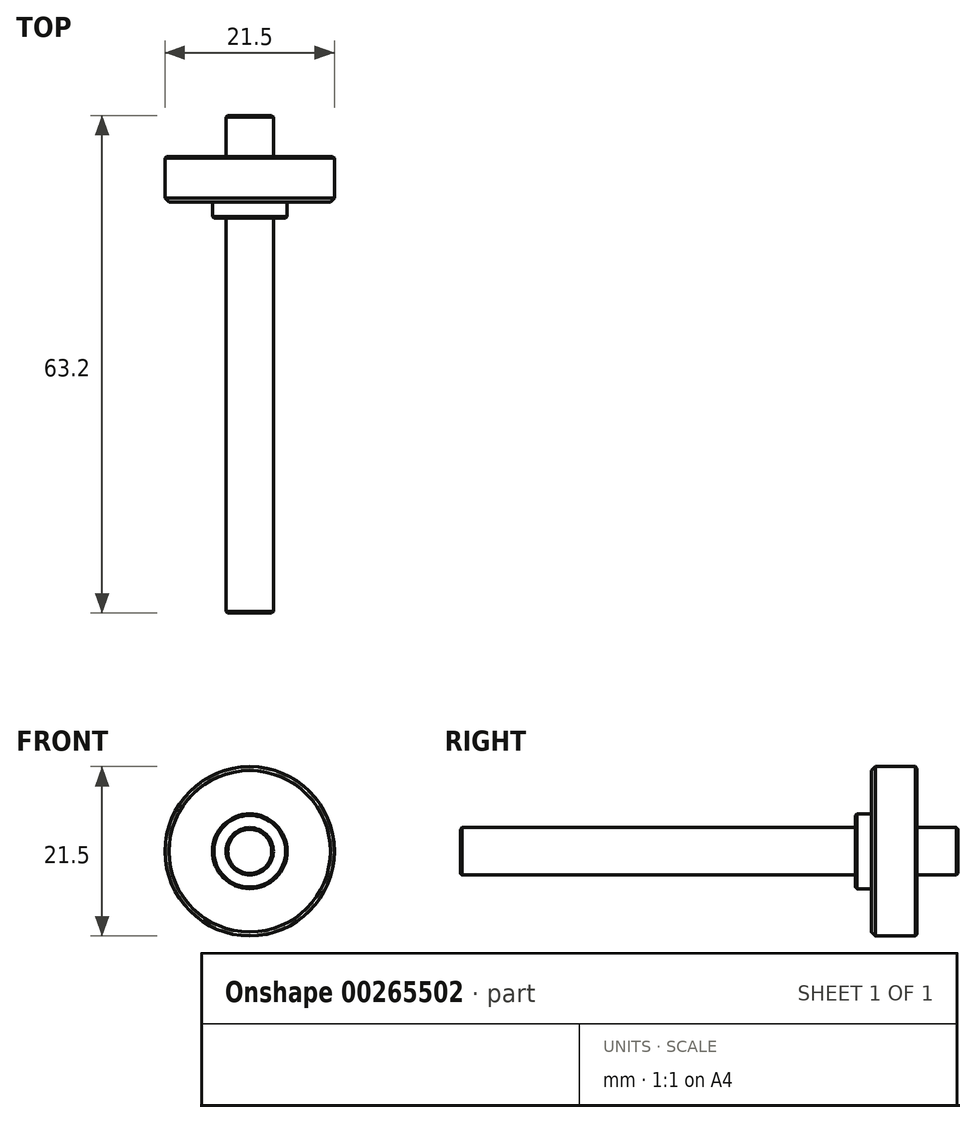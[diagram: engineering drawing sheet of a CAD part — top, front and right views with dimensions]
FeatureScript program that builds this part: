
annotation { "Feature Type Name" : "Feature", "Feature Type Description" : "" }
export const myFeature = defineFeature(function(context is Context, id is Id, definition is map)
    precondition{}
    {
        {
            var Q0;
            Q0=qCreatedBy(makeId("Front.planeOp"),FACE);
            var sketch = newSketch(context, id + "F0", { "sketchPlane" : qUnion([Q0])});
            skCircle(sketch, "E0", {"center": v(0, 0) * mm, "radius": 10.75 * mm});
            skSolve(sketch);
        }
        {
            var Q0;
            Q0=makeQuery(id+"F0.imprint","IMPRINT",FACE,{"disambiguationData":[TD([[makeQuery(id+"F0.imprint","IMPRINT",EDGE,{"derivedFrom":sQuery(id+"F0.wireOp",EDGE,"E0")}),1.0]])]});
            extrude(context, id + "F1", {"entities" : qUnion([Q0]), "depth" : 5.8 * mm});
        }
        {
            var Q0;
            Q0=makeQuery(id+"F1.opExtrude","CAP_FACE",FACE,{"disambiguationData":[OSD([sQuery(id+"F0.wireOp",EDGE,"E0")])],"isStart":false});
            var sketch = newSketch(context, id + "F2", { "sketchPlane" : qUnion([Q0])});
            skCircle(sketch, "E1", {"center": v(0, 0) * mm, "radius": 4.75 * mm});
            skSolve(sketch);
        }
        {
            var Q0;
            Q0=makeQuery(id+"F2.imprint","IMPRINT",FACE,{"disambiguationData":[TD([[makeQuery(id+"F2.imprint","IMPRINT",EDGE,{"derivedFrom":sQuery(id+"F2.wireOp",EDGE,"E1")}),1.0]])]});
            extrude(context, id + "F3", {"entities" : qUnion([Q0]), "operationType" : NewBodyOperationType.ADD, "depth" : 2 * mm});
        }
        {
            var Q0;
            Q0=makeQuery(id+"F3.opExtrude","CAP_FACE",FACE,{"disambiguationData":[OSD([sQuery(id+"F2.wireOp",EDGE,"E1")])],"isStart":false});
            var sketch = newSketch(context, id + "F4", { "sketchPlane" : qUnion([Q0])});
            skCircle(sketch, "E2", {"center": v(0, 0) * mm, "radius": 3 * mm});
            skSolve(sketch);
        }
        {
            var Q0;
            Q0=makeQuery(id+"F4.imprint","IMPRINT",FACE,{"disambiguationData":[TD([[makeQuery(id+"F4.imprint","IMPRINT",EDGE,{"derivedFrom":sQuery(id+"F4.wireOp",EDGE,"E2")}),1.0]])]});
            extrude(context, id + "F5", {"entities" : qUnion([Q0]), "operationType" : NewBodyOperationType.ADD, "depth" : 50.2 * mm});
        }
        {
            var Q0;
            Q0=makeQuery(id+"F1.opExtrude","CAP_FACE",FACE,{"disambiguationData":[OSD([sQuery(id+"F0.wireOp",EDGE,"E0")])],"isStart":true});
            var sketch = newSketch(context, id + "F6", { "sketchPlane" : qUnion([Q0])});
            skCircle(sketch, "E3", {"center": v(0, 0) * mm, "radius": 3 * mm});
            skSolve(sketch);
        }
        {
            var Q0;
            Q0=makeQuery(id+"F6.imprint","IMPRINT",FACE,{"disambiguationData":[TD([[makeQuery(id+"F6.imprint","IMPRINT",EDGE,{"derivedFrom":sQuery(id+"F6.wireOp",EDGE,"E3")}),1.0]])]});
            extrude(context, id + "F7", {"entities" : qUnion([Q0]), "operationType" : NewBodyOperationType.ADD, "depth" : 5.2 * mm});
        }
        {
            var Q0;
            Q0=makeQuery(id+"F1.opExtrude","CAP_EDGE",EDGE,{"disambiguationData":[OSD([sQuery(id+"F0.wireOp",EDGE,"E0")])],"isStart":false});
            chamfer(context, id + "F8", {"entities" : qUnion([Q0]), "width" : 0.5 * mm, "tangentPropagation" : true});
        }
        {
            var Q0;
            Q0=makeQuery(id+"F3.opExtrude","CAP_EDGE",EDGE,{"disambiguationData":[OSD([sQuery(id+"F2.wireOp",EDGE,"E1")])],"isStart":false});
            var Q1;
            Q1=makeQuery(id+"F5.opExtrude","CAP_EDGE",EDGE,{"disambiguationData":[OSD([sQuery(id+"F4.wireOp",EDGE,"E2")])],"isStart":false});
            var Q2;
            Q2=makeQuery(id+"F7.opExtrude","CAP_EDGE",EDGE,{"disambiguationData":[OSD([sQuery(id+"F6.wireOp",EDGE,"E3")])],"isStart":false});
            var Q3;
            Q3=makeQuery(id+"F1.opExtrude","CAP_EDGE",EDGE,{"disambiguationData":[OSD([sQuery(id+"F0.wireOp",EDGE,"E0")])],"isStart":true});
            chamfer(context, id + "F9", {"entities" : qUnion([Q0, Q1, Q2, Q3]), "width" : 0.2 * mm, "tangentPropagation" : true});
        }
    });
